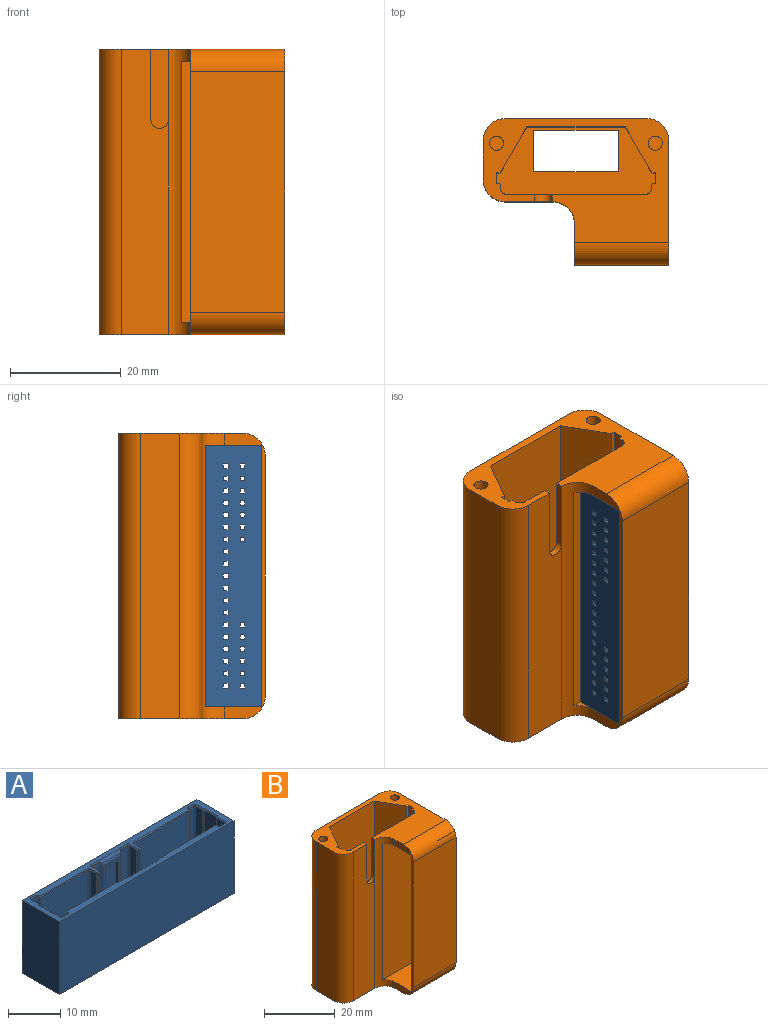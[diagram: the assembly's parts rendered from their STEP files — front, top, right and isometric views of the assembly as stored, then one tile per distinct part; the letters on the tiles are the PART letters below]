
ASSEMBLY  parts=2 mates=1
PART A: 258 faces, bbox 47.3x10.1x17.1 mm
  f0: plane 47.2x10mm, normal (0,0,-1), area 448.9mm2, adj f3,f4,f128,f129,f130,f131,f132,f133
  f1: plane 44.6x8.4mm, normal (0,0,1), area 288.9mm2, adj f9,f10,f22,f23,f34,f35,f39,f40
  f2: plane 47.2x10mm, normal (0,0,1), area 137.9mm2, adj f3,f4,f5,f6,f7,f8,f11,f12
  f3: plane 47.2x17mm, normal (0,-1,0), area 802.4mm2, adj f0,f2,f4,f128
  f4: plane 17x10mm, normal (1,0,0), area 170mm2, adj f0,f2,f3,f129
  f5: plane 2x0.2mm, normal (0,-0.71,0.71), area 0.5mm2, adj f2,f6,f81,f82
  f6: cone r=0.3mm half-angle=45deg, axis (0,0,1), area 0.1mm2, adj f2,f5,f7,f83
  f7: plane 2.1x0.2mm, normal (-0.71,0,0.71), area 0.6mm2, adj f2,f6,f8,f84
  f8: plane 0.38x0.38mm, normal (-0.5,-0.5,0.71), area 0.1mm2, adj f2,f7,f9,f11
  f9: plane 13.8x0.3mm, normal (-0.71,-0.71,0), area 5.9mm2, adj f1,f8,f10,f84
  f10: plane 13.8x0.4mm, normal (0,-1,0), area 5.5mm2, adj f1,f9,f11,f93
  f11: plane 0.4x0.2mm, normal (0,-0.71,0.71), area 0.1mm2, adj f2,f8,f10,f12
  f12: plane 0.38x0.38mm, normal (0.5,-0.5,0.71), area 0.1mm2, adj f2,f11,f13,f93
  f13: plane 1.6x0.2mm, normal (0.71,0,0.71), area 0.4mm2, adj f2,f12,f14,f94
  f14: cone r=0.4mm half-angle=45deg, axis (0,0,1), area 0.2mm2, adj f2,f13,f15,f95
  f15: plane 14.9x0.2mm, normal (0,-0.71,0.71), area 4.2mm2, adj f2,f14,f16,f96
  f16: cone r=0.2mm half-angle=45deg, axis (0,0,-1), area 0.1mm2, adj f2,f15,f17,f97
  f17: plane 0.2x0.2mm, normal (0.71,0,0.71), area 0.1mm2, adj f2,f16,f18,f98
  f18: cone r=0.4mm half-angle=45deg, axis (0,0,1), area 0.2mm2, adj f2,f17,f19,f99
  f19: plane 1.1x0.2mm, normal (0,-0.71,0.71), area 0.3mm2, adj f2,f18,f20,f100
  f20: cone r=0.4mm half-angle=45deg, axis (0,0,1), area 0.2mm2, adj f2,f19,f21,f101
  f21: plane 2x0.2mm, normal (-0.71,0,0.71), area 0.6mm2, adj f2,f20,f22,f24
  f22: plane 13.8x2mm, normal (-1,0,0), area 27.6mm2, adj f1,f21,f23,f101
  f23: plane 13.8x0.35mm, normal (-0.87,-0.5,0), area 5.5mm2, adj f1,f22,f24,f102
  f24: plane 0.4x0.4mm, normal (-0.61,-0.35,0.71), area 0.1mm2, adj f2,f21,f23,f25
  f25: plane 3.21x0.2mm, normal (-0.71,0,0.71), area 0.9mm2, adj f2,f24,f26,f102
  f26: plane 0.4x0.4mm, normal (-0.61,0.35,0.71), area 0.1mm2, adj f2,f25,f27,f103
  f27: plane 2x0.2mm, normal (-0.71,0,0.71), area 0.6mm2, adj f2,f26,f28,f104
  f28: cone r=0.4mm half-angle=45deg, axis (0,0,1), area 0.2mm2, adj f2,f27,f29,f105
  f29: plane 1.1x0.2mm, normal (0,0.71,0.71), area 0.3mm2, adj f2,f28,f30,f106
  f30: cone r=0.4mm half-angle=45deg, axis (0,0,1), area 0.2mm2, adj f2,f29,f31,f107
  f31: plane 0.2x0.2mm, normal (0.71,0,0.71), area 0.1mm2, adj f2,f30,f32,f108
  f32: cone r=0.2mm half-angle=45deg, axis (0,0,-1), area 0.1mm2, adj f2,f31,f33,f109
  f33: plane 13.5x0.2mm, normal (0,0.71,0.71), area 3.8mm2, adj f2,f32,f34,f36
  f34: plane 13.8x13.5mm, normal (0,1,0), area 186.3mm2, adj f1,f33,f35,f109
  f35: plane 13.8x0.35mm, normal (-0.5,0.87,0), area 5.5mm2, adj f1,f34,f36,f110
  f36: plane 0.4x0.4mm, normal (-0.35,0.61,0.71), area 0.1mm2, adj f2,f33,f35,f37
  f37: plane 1.91x0.2mm, normal (0,0.71,0.71), area 0.5mm2, adj f2,f36,f38,f110
  f38: plane 0.4x0.4mm, normal (-0.35,0.61,0.71), area 0.1mm2, adj f2,f37,f39,f41
  f39: plane 13.8x0.35mm, normal (-0.5,0.87,0), area 5.5mm2, adj f1,f38,f40,f110
  f40: plane 13.8x8.11mm, normal (0,1,0), area 111.9mm2, adj f1,f39,f41,f111
  f41: plane 8.21x0.2mm, normal (0,0.71,0.71), area 2.3mm2, adj f2,f38,f40,f42
  f42: plane 0.4x0.4mm, normal (0.35,0.61,0.71), area 0.1mm2, adj f2,f41,f43,f111
  f43: plane 1.91x0.2mm, normal (0,0.71,0.71), area 0.5mm2, adj f2,f42,f44,f112
  f44: plane 0.4x0.4mm, normal (0.35,0.61,0.71), area 0.1mm2, adj f2,f43,f45,f47
  f45: plane 13.8x0.35mm, normal (0.5,0.87,0), area 5.5mm2, adj f1,f44,f46,f112
  f46: plane 13.8x13.5mm, normal (0,1,0), area 186.3mm2, adj f1,f45,f47,f113
  f47: plane 13.5x0.2mm, normal (0,0.71,0.71), area 3.8mm2, adj f2,f44,f46,f48
  f48: cone r=0.2mm half-angle=45deg, axis (0,0,-1), area 0.1mm2, adj f2,f47,f49,f113
  f49: plane 0.2x0.2mm, normal (-0.71,0,0.71), area 0.1mm2, adj f2,f48,f50,f114
  f50: cone r=0.4mm half-angle=45deg, axis (0,0,1), area 0.2mm2, adj f2,f49,f51,f115
  f51: plane 1.1x0.2mm, normal (0,0.71,0.71), area 0.3mm2, adj f2,f50,f52,f116
  f52: cone r=0.4mm half-angle=45deg, axis (0,0,1), area 0.2mm2, adj f2,f51,f53,f117
  f53: plane 2x0.2mm, normal (0.71,0,0.71), area 0.6mm2, adj f2,f52,f54,f56
  f54: plane 13.8x2mm, normal (1,0,0), area 27.6mm2, adj f1,f53,f55,f117
  f55: plane 13.8x0.35mm, normal (0.87,0.5,0), area 5.5mm2, adj f1,f54,f56,f118
  f56: plane 0.4x0.4mm, normal (0.61,0.35,0.71), area 0.1mm2, adj f2,f53,f55,f57
  f57: plane 3.21x0.2mm, normal (0.71,0,0.71), area 0.9mm2, adj f2,f56,f58,f118
  f58: plane 0.4x0.4mm, normal (0.61,-0.35,0.71), area 0.1mm2, adj f2,f57,f59,f119
  f59: plane 2x0.2mm, normal (0.71,0,0.71), area 0.6mm2, adj f2,f58,f60,f120
  f60: cone r=0.4mm half-angle=45deg, axis (0,0,1), area 0.2mm2, adj f2,f59,f61,f121
  f61: plane 1.1x0.2mm, normal (0,-0.71,0.71), area 0.3mm2, adj f2,f60,f62,f122
  f62: cone r=0.4mm half-angle=45deg, axis (0,0,1), area 0.2mm2, adj f2,f61,f63,f123
  f63: plane 0.2x0.2mm, normal (-0.71,0,0.71), area 0.1mm2, adj f2,f62,f64,f124
  f64: cone r=0.2mm half-angle=45deg, axis (0,0,-1), area 0.1mm2, adj f2,f63,f65,f125
  f65: plane 12.7x0.2mm, normal (0,-0.71,0.71), area 3.6mm2, adj f2,f64,f66,f126
  f66: cone r=0.4mm half-angle=45deg, axis (0,0,1), area 0.2mm2, adj f2,f65,f67,f127
  f67: plane 1.6x0.2mm, normal (-0.71,0,0.71), area 0.4mm2, adj f2,f66,f68,f70
  f68: plane 13.8x1.6mm, normal (-1,0,0), area 22.1mm2, adj f1,f67,f69,f127
  f69: plane 13.8x0.3mm, normal (-0.71,-0.71,0), area 5.9mm2, adj f1,f68,f70,f72
  f70: plane 0.38x0.38mm, normal (-0.5,-0.5,0.71), area 0.1mm2, adj f2,f67,f69,f71
  f71: plane 0.4x0.2mm, normal (0,-0.71,0.71), area 0.1mm2, adj f2,f70,f72,f74
  f72: plane 13.8x0.4mm, normal (0,-1,0), area 5.5mm2, adj f1,f69,f71,f73
  f73: plane 13.8x0.3mm, normal (0.71,-0.71,0), area 5.9mm2, adj f1,f72,f74,f86
  f74: plane 0.38x0.38mm, normal (0.5,-0.5,0.71), area 0.1mm2, adj f2,f71,f73,f75
  f75: plane 2.1x0.2mm, normal (0.71,0,0.71), area 0.6mm2, adj f2,f74,f76,f86
  f76: cone r=0.3mm half-angle=45deg, axis (0,0,1), area 0.1mm2, adj f2,f75,f77,f85
  f77: plane 2x0.2mm, normal (0,-0.71,0.71), area 0.5mm2, adj f2,f76,f78,f79
  f78: plane 13.8x2mm, normal (0,-1,0), area 27.6mm2, adj f1,f77,f79,f85
  f79: plane 14.09x0.79mm, normal (-0.71,-0.71,0), area 9.5mm2, adj f1,f2,f77,f78,f80,f87,f92
  f80: plane 5.86x0.64mm, normal (0,-0.82,0.57), area 4.2mm2, adj f2,f79,f81,f92
  f81: plane 14.09x0.79mm, normal (0.71,-0.71,0), area 9.5mm2, adj f1,f2,f5,f80,f82,f87,f92
  f82: plane 13.8x2mm, normal (0,-1,0), area 27.6mm2, adj f1,f5,f81,f83
  f83: cylinder r=0.2mm len=13.8mm, axis (0,0,-1), area 4.3mm2, adj f1,f6,f82,f84
  f84: plane 13.8x2.1mm, normal (-1,0,0), area 29mm2, adj f1,f7,f9,f83
  f85: cylinder r=0.2mm len=13.8mm, axis (0,0,-1), area 4.3mm2, adj f1,f76,f78,f86
  f86: plane 13.8x2.1mm, normal (1,0,0), area 29mm2, adj f1,f73,f75,f85
  f87: plane 12.78x4.6mm, normal (0,-1,0), area 15.6mm2, adj f1,f79,f81,f88,f90,f91,f92
  f88: plane 12.13x0.9mm, normal (-1,0,0), area 10.9mm2, adj f1,f87,f89,f91
  f89: plane 12.13x3.6mm, normal (0,-1,0), area 43.7mm2, adj f1,f88,f90,f91
  f90: plane 12.13x0.9mm, normal (1,0,0), area 10.9mm2, adj f1,f87,f89,f91
  f91: plane 3.6x0.9mm, normal (0,0.14,-0.99), area 3.3mm2, adj f87,f88,f89,f90
  f92: cylinder r=1mm len=4.96mm, axis (1,0,0), area 2.9mm2, adj f79,f80,f81,f87
  f93: plane 13.8x0.3mm, normal (0.71,-0.71,0), area 5.9mm2, adj f1,f10,f12,f94
  f94: plane 13.8x1.6mm, normal (1,0,0), area 22.1mm2, adj f1,f13,f93,f95
  f95: cylinder r=0.3mm len=13.8mm, axis (0,0,1), area 6.5mm2, adj f1,f14,f94,f96
  f96: plane 14.9x13.8mm, normal (0,-1,0), area 205.6mm2, adj f1,f15,f95,f97
  f97: cylinder r=0.3mm len=13.8mm, axis (0,0,1), area 6.5mm2, adj f1,f16,f96,f98
  f98: plane 13.8x0.2mm, normal (1,0,0), area 2.8mm2, adj f1,f17,f97,f99
  f99: cylinder r=0.3mm len=13.8mm, axis (0,0,1), area 6.5mm2, adj f1,f18,f98,f100
  f100: plane 13.8x1.1mm, normal (0,-1,0), area 15.2mm2, adj f1,f19,f99,f101
  f101: cylinder r=0.3mm len=13.8mm, axis (0,0,1), area 6.5mm2, adj f1,f20,f22,f100
  f102: plane 13.8x3.11mm, normal (-1,0,0), area 42.9mm2, adj f1,f23,f25,f103
  f103: plane 13.8x0.35mm, normal (-0.87,0.5,0), area 5.5mm2, adj f1,f26,f102,f104
  f104: plane 13.8x2mm, normal (-1,0,0), area 27.6mm2, adj f1,f27,f103,f105
  f105: cylinder r=0.3mm len=13.8mm, axis (0,0,1), area 6.5mm2, adj f1,f28,f104,f106
  f106: plane 13.8x1.1mm, normal (0,1,0), area 15.2mm2, adj f1,f29,f105,f107
  f107: cylinder r=0.3mm len=13.8mm, axis (0,0,1), area 6.5mm2, adj f1,f30,f106,f108
  f108: plane 13.8x0.2mm, normal (1,0,0), area 2.8mm2, adj f1,f31,f107,f109
  f109: cylinder r=0.3mm len=13.8mm, axis (0,0,1), area 6.5mm2, adj f1,f32,f34,f108
  f110: plane 13.8x1.85mm, normal (0,1,0), area 25.6mm2, adj f1,f35,f37,f39
  f111: plane 13.8x0.35mm, normal (0.5,0.87,0), area 5.5mm2, adj f1,f40,f42,f112
  f112: plane 13.8x1.85mm, normal (0,1,0), area 25.6mm2, adj f1,f43,f45,f111
  f113: cylinder r=0.3mm len=13.8mm, axis (0,0,1), area 6.5mm2, adj f1,f46,f48,f114
  f114: plane 13.8x0.2mm, normal (-1,0,0), area 2.8mm2, adj f1,f49,f113,f115
  f115: cylinder r=0.3mm len=13.8mm, axis (0,0,1), area 6.5mm2, adj f1,f50,f114,f116
  f116: plane 13.8x1.1mm, normal (0,1,0), area 15.2mm2, adj f1,f51,f115,f117
  f117: cylinder r=0.3mm len=13.8mm, axis (0,0,1), area 6.5mm2, adj f1,f52,f54,f116
  f118: plane 13.8x3.11mm, normal (1,0,0), area 42.9mm2, adj f1,f55,f57,f119
  f119: plane 13.8x0.35mm, normal (0.87,-0.5,0), area 5.5mm2, adj f1,f58,f118,f120
  f120: plane 13.8x2mm, normal (1,0,0), area 27.6mm2, adj f1,f59,f119,f121
  f121: cylinder r=0.3mm len=13.8mm, axis (0,0,1), area 6.5mm2, adj f1,f60,f120,f122
  f122: plane 13.8x1.1mm, normal (0,-1,0), area 15.2mm2, adj f1,f61,f121,f123
  f123: cylinder r=0.3mm len=13.8mm, axis (0,0,1), area 6.5mm2, adj f1,f62,f122,f124
  f124: plane 13.8x0.2mm, normal (-1,0,0), area 2.8mm2, adj f1,f63,f123,f125
  f125: cylinder r=0.3mm len=13.8mm, axis (0,0,1), area 6.5mm2, adj f1,f64,f124,f126
  f126: plane 13.8x12.7mm, normal (0,-1,0), area 175.3mm2, adj f1,f65,f125,f127
  f127: cylinder r=0.3mm len=13.8mm, axis (0,0,1), area 6.5mm2, adj f1,f66,f68,f126
  f128: plane 17x10mm, normal (-1,0,0), area 170mm2, adj f0,f2,f3,f129
  f129: plane 47.2x17mm, normal (0,1,0), area 802.4mm2, adj f0,f2,f4,f128
  f130: plane 3x0.85mm, normal (0,-1,0), area 2.6mm2, adj f0,f1,f131,f133
  f131: plane 3x0.85mm, normal (-1,0,0), area 2.6mm2, adj f0,f1,f130,f132
  f132: plane 3x0.85mm, normal (0,1,0), area 2.6mm2, adj f0,f1,f131,f133
  f133: plane 3x0.85mm, normal (1,0,0), area 2.6mm2, adj f0,f1,f130,f132
  f134: plane 3x0.85mm, normal (0,1,0), area 2.6mm2, adj f0,f1,f135,f137
  f135: plane 3x0.85mm, normal (1,0,0), area 2.6mm2, adj f0,f1,f134,f136
  f136: plane 3x0.85mm, normal (0,-1,0), area 2.6mm2, adj f0,f1,f135,f137
  f137: plane 3x0.85mm, normal (-1,0,0), area 2.6mm2, adj f0,f1,f134,f136
  f138: plane 3x0.85mm, normal (0,-1,0), area 2.6mm2, adj f0,f1,f139,f141
  f139: plane 3x0.85mm, normal (-1,0,0), area 2.6mm2, adj f0,f1,f138,f140
  f140: plane 3x0.85mm, normal (0,1,0), area 2.6mm2, adj f0,f1,f139,f141
  f141: plane 3x0.85mm, normal (1,0,0), area 2.6mm2, adj f0,f1,f138,f140
  f142: plane 3x0.85mm, normal (0,-1,0), area 2.5mm2, adj f0,f1,f143,f145
  f143: plane 3x0.85mm, normal (-1,0,0), area 2.6mm2, adj f0,f1,f142,f144
  f144: plane 3x0.85mm, normal (0,1,0), area 2.5mm2, adj f0,f1,f143,f145
  f145: plane 3x0.85mm, normal (1,0,0), area 2.6mm2, adj f0,f1,f142,f144
  f146: plane 3x0.85mm, normal (0,-1,0), area 2.6mm2, adj f0,f1,f147,f149
  f147: plane 3x0.85mm, normal (-1,0,0), area 2.6mm2, adj f0,f1,f146,f148
  f148: plane 3x0.85mm, normal (0,1,0), area 2.6mm2, adj f0,f1,f147,f149
  f149: plane 3x0.85mm, normal (1,0,0), area 2.6mm2, adj f0,f1,f146,f148
  f150: plane 3x0.85mm, normal (0,-1,0), area 2.6mm2, adj f0,f1,f151,f153
  f151: plane 3x0.85mm, normal (-1,0,0), area 2.6mm2, adj f0,f1,f150,f152
  f152: plane 3x0.85mm, normal (0,1,0), area 2.6mm2, adj f0,f1,f151,f153
  f153: plane 3x0.85mm, normal (1,0,0), area 2.6mm2, adj f0,f1,f150,f152
  f154: plane 3x0.85mm, normal (0,-1,0), area 2.6mm2, adj f0,f1,f155,f157
  f155: plane 3x0.85mm, normal (-1,0,0), area 2.6mm2, adj f0,f1,f154,f156
  f156: plane 3x0.85mm, normal (0,1,0), area 2.6mm2, adj f0,f1,f155,f157
  f157: plane 3x0.85mm, normal (1,0,0), area 2.6mm2, adj f0,f1,f154,f156
  f158: plane 3x0.85mm, normal (0,-1,0), area 2.6mm2, adj f0,f1,f159,f161
  f159: plane 3x0.85mm, normal (-1,0,0), area 2.6mm2, adj f0,f1,f158,f160
  f160: plane 3x0.85mm, normal (0,1,0), area 2.6mm2, adj f0,f1,f159,f161
  f161: plane 3x0.85mm, normal (1,0,0), area 2.6mm2, adj f0,f1,f158,f160
  f162: plane 3x0.85mm, normal (0,-1,0), area 2.6mm2, adj f0,f1,f163,f165
  f163: plane 3x0.85mm, normal (-1,0,0), area 2.6mm2, adj f0,f1,f162,f164
  f164: plane 3x0.85mm, normal (0,1,0), area 2.6mm2, adj f0,f1,f163,f165
  f165: plane 3x0.85mm, normal (1,0,0), area 2.6mm2, adj f0,f1,f162,f164
  f166: plane 3x0.85mm, normal (0,-1,0), area 2.6mm2, adj f0,f1,f167,f169
  f167: plane 3x0.85mm, normal (-1,0,0), area 2.6mm2, adj f0,f1,f166,f168
  f168: plane 3x0.85mm, normal (0,1,0), area 2.6mm2, adj f0,f1,f167,f169
  f169: plane 3x0.85mm, normal (1,0,0), area 2.6mm2, adj f0,f1,f166,f168
  f170: plane 3x0.85mm, normal (0,-1,0), area 2.6mm2, adj f0,f1,f171,f173
  f171: plane 3x0.85mm, normal (-1,0,0), area 2.6mm2, adj f0,f1,f170,f172
  f172: plane 3x0.85mm, normal (0,1,0), area 2.6mm2, adj f0,f1,f171,f173
  f173: plane 3x0.85mm, normal (1,0,0), area 2.6mm2, adj f0,f1,f170,f172
  f174: plane 3x0.85mm, normal (0,-1,0), area 2.6mm2, adj f0,f1,f175,f177
  f175: plane 3x0.85mm, normal (-1,0,0), area 2.6mm2, adj f0,f1,f174,f176
  f176: plane 3x0.85mm, normal (0,1,0), area 2.6mm2, adj f0,f1,f175,f177
  f177: plane 3x0.85mm, normal (1,0,0), area 2.6mm2, adj f0,f1,f174,f176
  f178: plane 3x0.85mm, normal (0,-1,0), area 2.6mm2, adj f0,f1,f179,f181
  f179: plane 3x0.85mm, normal (-1,0,0), area 2.6mm2, adj f0,f1,f178,f180
  f180: plane 3x0.85mm, normal (0,1,0), area 2.6mm2, adj f0,f1,f179,f181
  f181: plane 3x0.85mm, normal (1,0,0), area 2.6mm2, adj f0,f1,f178,f180
  f182: plane 3x0.85mm, normal (0,-1,0), area 2.6mm2, adj f0,f1,f183,f185
  f183: plane 3x0.85mm, normal (-1,0,0), area 2.6mm2, adj f0,f1,f182,f184
  f184: plane 3x0.85mm, normal (0,1,0), area 2.6mm2, adj f0,f1,f183,f185
  f185: plane 3x0.85mm, normal (1,0,0), area 2.6mm2, adj f0,f1,f182,f184
  f186: plane 3x0.85mm, normal (0,-1,0), area 2.6mm2, adj f0,f1,f187,f189
  f187: plane 3x0.85mm, normal (-1,0,0), area 2.6mm2, adj f0,f1,f186,f188
  f188: plane 3x0.85mm, normal (0,1,0), area 2.6mm2, adj f0,f1,f187,f189
  f189: plane 3x0.85mm, normal (1,0,0), area 2.6mm2, adj f0,f1,f186,f188
  f190: plane 3x0.85mm, normal (0,-1,0), area 2.6mm2, adj f0,f1,f191,f193
  f191: plane 3x0.85mm, normal (-1,0,0), area 2.6mm2, adj f0,f1,f190,f192
  f192: plane 3x0.85mm, normal (0,1,0), area 2.6mm2, adj f0,f1,f191,f193
  f193: plane 3x0.85mm, normal (1,0,0), area 2.6mm2, adj f0,f1,f190,f192
  f194: plane 3x0.85mm, normal (0,-1,0), area 2.6mm2, adj f0,f1,f195,f197
  f195: plane 3x0.85mm, normal (-1,0,0), area 2.6mm2, adj f0,f1,f194,f196
  f196: plane 3x0.85mm, normal (0,1,0), area 2.6mm2, adj f0,f1,f195,f197
  f197: plane 3x0.85mm, normal (1,0,0), area 2.6mm2, adj f0,f1,f194,f196
  f198: plane 3x0.85mm, normal (0,-1,0), area 2.5mm2, adj f0,f1,f199,f201
  f199: plane 3x0.85mm, normal (-1,0,0), area 2.6mm2, adj f0,f1,f198,f200
  f200: plane 3x0.85mm, normal (0,1,0), area 2.5mm2, adj f0,f1,f199,f201
  f201: plane 3x0.85mm, normal (1,0,0), area 2.6mm2, adj f0,f1,f198,f200
  f202: plane 3x0.85mm, normal (0,-1,0), area 2.6mm2, adj f0,f1,f203,f205
  f203: plane 3x0.85mm, normal (-1,0,0), area 2.6mm2, adj f0,f1,f202,f204
  f204: plane 3x0.85mm, normal (0,1,0), area 2.6mm2, adj f0,f1,f203,f205
  f205: plane 3x0.85mm, normal (1,0,0), area 2.6mm2, adj f0,f1,f202,f204
  f206: plane 3x0.85mm, normal (0,-1,0), area 2.6mm2, adj f0,f1,f207,f209
  f207: plane 3x0.85mm, normal (-1,0,0), area 2.6mm2, adj f0,f1,f206,f208
  f208: plane 3x0.85mm, normal (0,1,0), area 2.6mm2, adj f0,f1,f207,f209
  f209: plane 3x0.85mm, normal (1,0,0), area 2.6mm2, adj f0,f1,f206,f208
  f210: plane 3x0.85mm, normal (0,-1,0), area 2.6mm2, adj f0,f1,f211,f213
  f211: plane 3x0.85mm, normal (-1,0,0), area 2.6mm2, adj f0,f1,f210,f212
  f212: plane 3x0.85mm, normal (0,1,0), area 2.6mm2, adj f0,f1,f211,f213
  f213: plane 3x0.85mm, normal (1,0,0), area 2.6mm2, adj f0,f1,f210,f212
  f214: plane 3x0.85mm, normal (0,-1,0), area 2.6mm2, adj f0,f1,f215,f217
  f215: plane 3x0.85mm, normal (-1,0,0), area 2.6mm2, adj f0,f1,f214,f216
  f216: plane 3x0.85mm, normal (0,1,0), area 2.6mm2, adj f0,f1,f215,f217
  f217: plane 3x0.85mm, normal (1,0,0), area 2.6mm2, adj f0,f1,f214,f216
  f218: plane 3x0.85mm, normal (0,-1,0), area 2.6mm2, adj f0,f1,f219,f221
  f219: plane 3x0.85mm, normal (-1,0,0), area 2.6mm2, adj f0,f1,f218,f220
  f220: plane 3x0.85mm, normal (0,1,0), area 2.6mm2, adj f0,f1,f219,f221
  f221: plane 3x0.85mm, normal (1,0,0), area 2.6mm2, adj f0,f1,f218,f220
  f222: plane 3x0.85mm, normal (0,-1,0), area 2.6mm2, adj f0,f1,f223,f225
  f223: plane 3x0.85mm, normal (-1,0,0), area 2.6mm2, adj f0,f1,f222,f224
  f224: plane 3x0.85mm, normal (0,1,0), area 2.6mm2, adj f0,f1,f223,f225
  f225: plane 3x0.85mm, normal (1,0,0), area 2.6mm2, adj f0,f1,f222,f224
  f226: plane 3x0.85mm, normal (0,-1,0), area 2.6mm2, adj f0,f1,f227,f229
  f227: plane 3x0.85mm, normal (-1,0,0), area 2.6mm2, adj f0,f1,f226,f228
  f228: plane 3x0.85mm, normal (0,1,0), area 2.6mm2, adj f0,f1,f227,f229
  f229: plane 3x0.85mm, normal (1,0,0), area 2.6mm2, adj f0,f1,f226,f228
  f230: plane 3x0.85mm, normal (0,-1,0), area 2.5mm2, adj f0,f1,f231,f233
  f231: plane 3x0.85mm, normal (-1,0,0), area 2.6mm2, adj f0,f1,f230,f232
  f232: plane 3x0.85mm, normal (0,1,0), area 2.5mm2, adj f0,f1,f231,f233
  f233: plane 3x0.85mm, normal (1,0,0), area 2.6mm2, adj f0,f1,f230,f232
  f234: plane 3x0.85mm, normal (0,-1,0), area 2.6mm2, adj f0,f1,f235,f237
  f235: plane 3x0.85mm, normal (-1,0,0), area 2.6mm2, adj f0,f1,f234,f236
  f236: plane 3x0.85mm, normal (0,1,0), area 2.6mm2, adj f0,f1,f235,f237
  f237: plane 3x0.85mm, normal (1,0,0), area 2.6mm2, adj f0,f1,f234,f236
  f238: plane 3x0.85mm, normal (0,-1,0), area 2.6mm2, adj f0,f1,f239,f241
  f239: plane 3x0.85mm, normal (-1,0,0), area 2.6mm2, adj f0,f1,f238,f240
  f240: plane 3x0.85mm, normal (0,1,0), area 2.6mm2, adj f0,f1,f239,f241
  f241: plane 3x0.85mm, normal (1,0,0), area 2.6mm2, adj f0,f1,f238,f240
  f242: plane 3x0.85mm, normal (0,-1,0), area 2.6mm2, adj f0,f1,f243,f245
  f243: plane 3x0.85mm, normal (-1,0,0), area 2.6mm2, adj f0,f1,f242,f244
  f244: plane 3x0.85mm, normal (0,1,0), area 2.6mm2, adj f0,f1,f243,f245
  f245: plane 3x0.85mm, normal (1,0,0), area 2.6mm2, adj f0,f1,f242,f244
  f246: plane 3x0.85mm, normal (0,-1,0), area 2.6mm2, adj f0,f1,f247,f249
  f247: plane 3x0.85mm, normal (-1,0,0), area 2.6mm2, adj f0,f1,f246,f248
  f248: plane 3x0.85mm, normal (0,1,0), area 2.6mm2, adj f0,f1,f247,f249
  f249: plane 3x0.85mm, normal (1,0,0), area 2.6mm2, adj f0,f1,f246,f248
  f250: plane 3x0.85mm, normal (0,-1,0), area 2.5mm2, adj f0,f1,f251,f253
  f251: plane 3x0.85mm, normal (-1,0,0), area 2.6mm2, adj f0,f1,f250,f252
  f252: plane 3x0.85mm, normal (0,1,0), area 2.5mm2, adj f0,f1,f251,f253
  f253: plane 3x0.85mm, normal (1,0,0), area 2.6mm2, adj f0,f1,f250,f252
  f254: plane 3x0.85mm, normal (0,-1,0), area 2.6mm2, adj f0,f1,f255,f257
  f255: plane 3x0.85mm, normal (-1,0,0), area 2.6mm2, adj f0,f1,f254,f256
  f256: plane 3x0.85mm, normal (0,1,0), area 2.6mm2, adj f0,f1,f255,f257
  f257: plane 3x0.85mm, normal (1,0,0), area 2.6mm2, adj f0,f1,f254,f256
PART B: 44 faces, bbox 33.5x26.4x51.5 mm
  f0: plane 33.5x22.43mm, normal (0,0,1), area 309.9mm2, adj f1,f2,f3,f5,f7,f8,f9,f10
  f1: plane 50x24.81mm, normal (0,1,0), area 1196.2mm2, adj f0,f20,f39,f40,f41,f42,f43
  f2: plane 51.5x7.43mm, normal (-1,0,0), area 58.8mm2, adj f0,f4,f6,f29,f30,f32,f33,f37
  f3: plane 51.5x22.43mm, normal (1,0,0), area 676.3mm2, adj f0,f4,f6,f29,f30,f31,f32,f34
  f4: plane 33.5x22.43mm, normal (0,0,-1), area 507.6mm2, adj f2,f3,f5,f7,f8,f21,f22,f23
  f5: plane 51.5x8.5mm, normal (0,-1,0), area 393.5mm2, adj f0,f4,f33,f36,f39,f40
  f6: plane 43.5x17mm, normal (0,-1,0), area 739.5mm2, adj f2,f3,f37,f38
  f7: plane 51.5x25.5mm, normal (0,1,0), area 1313.2mm2, adj f0,f4,f34,f35
  f8: plane 51.5x7mm, normal (-1,0,0), area 360.5mm2, adj f0,f4,f35,f36
  f9: plane 50x8.26mm, normal (0.87,-0.5,0), area 477mm2, adj f0,f10,f19,f20
  f10: plane 50x0.7mm, normal (0,-1,0), area 35mm2, adj f0,f9,f11,f20
  f11: plane 50x2mm, normal (1,0,0), area 100mm2, adj f0,f10,f12,f20
  f12: plane 50x0.7mm, normal (0,1,0), area 35mm2, adj f0,f11,f13,f20
  f13: plane 50x0.73mm, normal (1,0,0), area 36.5mm2, adj f0,f12,f20,f42
  f14: plane 50x0.73mm, normal (-1,0,0), area 36.5mm2, adj f0,f15,f20,f43
  f15: plane 50x0.7mm, normal (0,1,0), area 35mm2, adj f0,f14,f16,f20
  f16: plane 50x2mm, normal (-1,0,0), area 100mm2, adj f0,f15,f17,f20
  f17: plane 50x0.7mm, normal (0,-1,0), area 35mm2, adj f0,f16,f18,f20
  f18: plane 50x8.26mm, normal (-0.87,-0.5,0), area 477mm2, adj f0,f17,f19,f20
  f19: plane 50x17.8mm, normal (0,-1,0), area 889.9mm2, adj f0,f9,f18,f20
  f20: plane 28.75x12.26mm, normal (0,0,1), area 183.5mm2, adj f1,f9,f10,f11,f12,f13,f14,f15
  f21: plane 15.25x1.5mm, normal (0,-1,0), area 22.9mm2, adj f4,f20,f22,f24
  f22: plane 7.5x1.5mm, normal (1,0,0), area 11.3mm2, adj f4,f20,f21,f23
  f23: plane 15.25x1.5mm, normal (0,1,0), area 22.9mm2, adj f4,f20,f22,f24
  f24: plane 7.5x1.5mm, normal (-1,0,0), area 11.3mm2, adj f4,f20,f21,f23
  f25: cylinder r=1.27mm len=8mm, axis (0,0,1), area 63.8mm2, adj f0,f26
  f26: plane 2.54x2.54mm, normal (0,0,1), area 5.1mm2, adj f25
  f27: cylinder r=1.27mm len=8mm, axis (0,0,1), area 63.8mm2, adj f0,f28
  f28: plane 2.54x2.54mm, normal (0,0,1), area 5.1mm2, adj f27
  f29: plane 47.2x17mm, normal (0,1,0), area 802.4mm2, adj f2,f3,f30,f32
  f30: plane 18.72x10mm, normal (0,0,1), area 171.7mm2, adj f2,f3,f29,f31,f33
  f31: plane 47.2x18.72mm, normal (0,-1,0), area 883.5mm2, adj f3,f30,f32,f33
  f32: plane 18.72x10mm, normal (0,0,-1), area 171.7mm2, adj f2,f3,f29,f31,f33
  f33: cylinder r=4mm len=51.5mm, axis (0,0,1), area 141.7mm2, adj f0,f2,f4,f5,f30,f31,f32,f41
  f34: cylinder r=4mm len=51.5mm, axis (0,0,-1), area 323.6mm2, adj f0,f3,f4,f7
  f35: cylinder r=4mm len=51.5mm, axis (0,0,1), area 323.6mm2, adj f0,f4,f7,f8
  f36: cylinder r=4mm len=51.5mm, axis (0,0,-1), area 323.6mm2, adj f0,f4,f5,f8
  f37: cylinder r=4mm len=17mm, axis (1,0,0), area 106.8mm2, adj f2,f3,f4,f6
  f38: cylinder r=4mm len=17mm, axis (-1,0,0), area 106.8mm2, adj f0,f2,f3,f6
  f39: cylinder r=1.59mm len=3.18mm, axis (0,-1,0), area 6.2mm2, adj f1,f5,f40,f41
  f40: plane 12.7x1.24mm, normal (1,0,0), area 15.8mm2, adj f0,f1,f5,f39
  f41: plane 12.7x1.24mm, normal (-1,0,0), area 15.8mm2, adj f0,f1,f33,f39
  f42: cylinder r=1.27mm len=50mm, axis (0,0,-1), area 99.7mm2, adj f0,f1,f13,f20
  f43: cylinder r=1.27mm len=50mm, axis (0,0,-1), area 99.7mm2, adj f0,f1,f14,f20
PLACE A rot(axis=(0.71,0,0.71),180deg) t=(-5.33,-4.89,24.54)mm
PLACE B t=(-22.08,8.33,-1.21)mm
MATE fastened A.f129 <-> B.f29  axis (0,-1,0) through (-13.83,-9.89,24.54)mm
